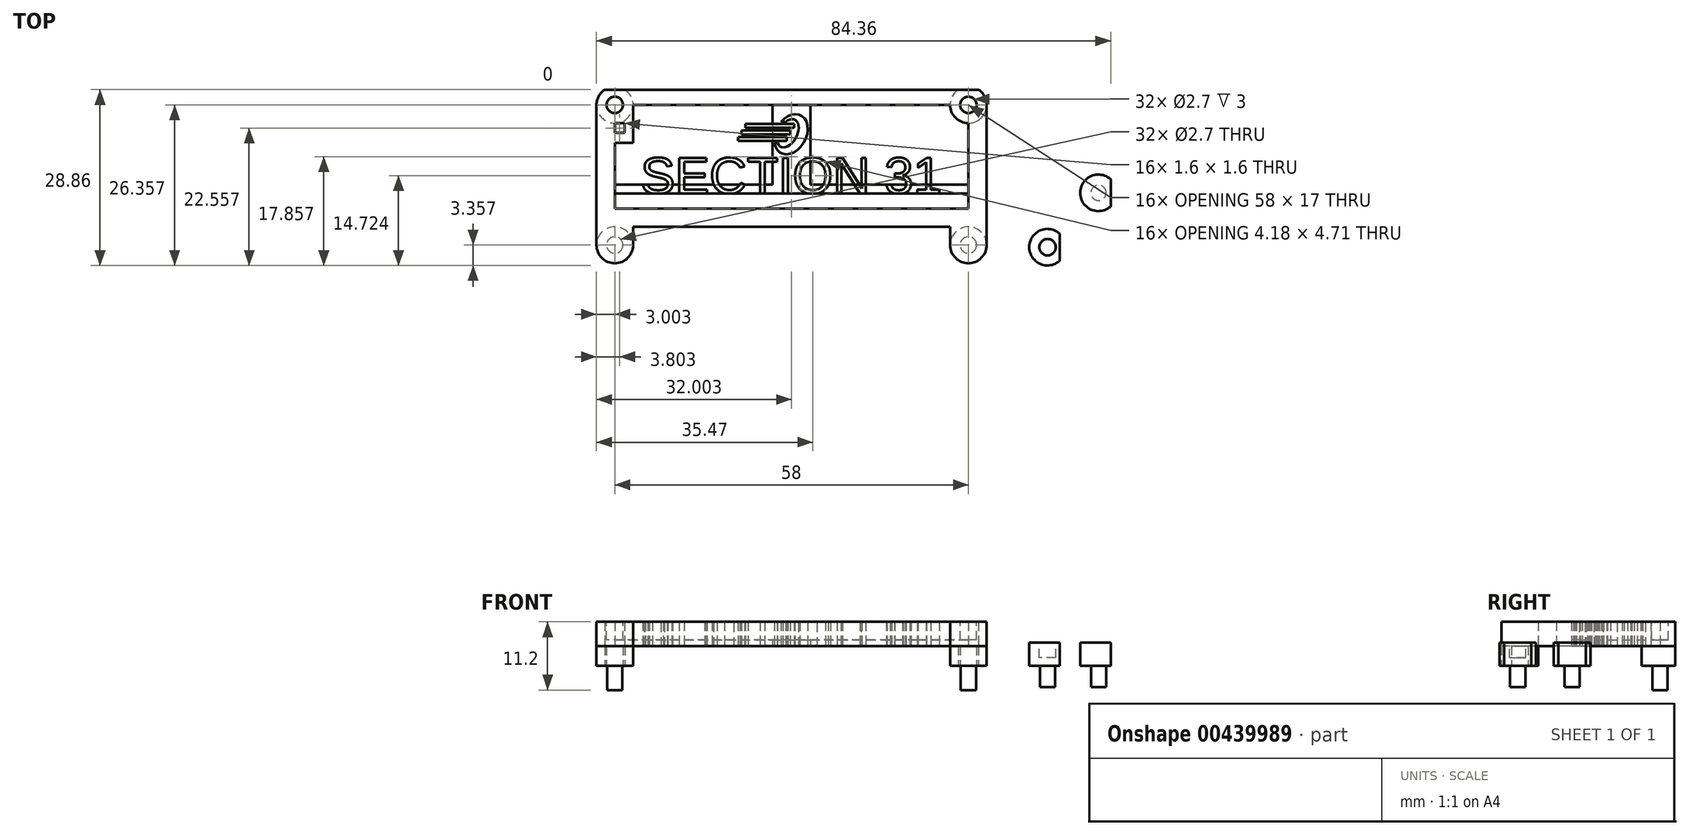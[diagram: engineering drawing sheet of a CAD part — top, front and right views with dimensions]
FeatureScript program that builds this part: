
annotation { "Feature Type Name" : "Feature", "Feature Type Description" : "" }
export const myFeature = defineFeature(function(context is Context, id is Id, definition is map)
    precondition{}
    {
        {
            var Q0;
            Q0=qCreatedBy(makeId("Top.planeOp"),FACE);
            var sketch = newSketch(context, id + "F0", { "sketchPlane" : qUnion([Q0])});
            skArc(sketch, "E0", {"start": v(2, 2.24) * mm, "mid": v(-3, 0) * mm, "end": v(2, -2.24) * mm});
            skCircle(sketch, "E1", {"center": v(0, 0) * mm, "radius": 1.25 * mm});
            skLineSegment(sketch, "E2", {"start": v(2, 2.24) * mm, "end": v(2, -2.24) * mm});
            skPoint(sketch, "E3", {"position": v(-9.49, 26.86) * mm});
            skLineSegment(sketch, "E4.bottom", {"start": v(-9.49, 26.86) * mm, "end": v(-74.49, 26.86) * mm});
            skLineSegment(sketch, "E4.top", {"start": v(-9.49, -3.14) * mm, "end": v(-74.49, -3.14) * mm});
            skLineSegment(sketch, "E4.left", {"start": v(-9.49, 26.86) * mm, "end": v(-9.49, -3.14) * mm});
            skLineSegment(sketch, "E4.right", {"start": v(-74.49, 26.86) * mm, "end": v(-74.49, -3.14) * mm});
            skLineSegment(sketch, "E5", {"start": v(-41.99, 26.86) * mm, "end": v(-41.99, -3.14) * mm, "construction": true});
            skLineSegment(sketch, "E6", {"start": v(-74.49, 11.86) * mm, "end": v(-9.49, 11.86) * mm, "construction": true});
            skPoint(sketch, "E7", {"position": v(-12.99, 23.36) * mm});
            skPoint(sketch, "E8", {"position": v(-70.99, 23.36) * mm});
            skPoint(sketch, "E9", {"position": v(-70.99, 0.36) * mm});
            skPoint(sketch, "E10", {"position": v(-12.99, 0.36) * mm});
            skArc(sketch, "E11", {"start": v(-14.65, 25.86) * mm, "mid": v(-12.99, 20.36) * mm, "end": v(-11.33, 25.86) * mm});
            skArc(sketch, "E12", {"start": v(-72.65, 25.86) * mm, "mid": v(-70.99, 20.36) * mm, "end": v(-69.33, 25.86) * mm});
            skCircle(sketch, "E13", {"center": v(-70.99, 0.36) * mm, "radius": 3 * mm});
            skCircle(sketch, "E14", {"center": v(-12.99, 0.36) * mm, "radius": 3 * mm});
            skCircle(sketch, "E15", {"center": v(-70.99, 23.36) * mm, "radius": 1.25 * mm});
            skCircle(sketch, "E16", {"center": v(-12.99, 23.36) * mm, "radius": 1.25 * mm});
            skCircle(sketch, "E17", {"center": v(-70.99, 0.36) * mm, "radius": 1.35 * mm});
            skCircle(sketch, "E18", {"center": v(-12.99, 0.36) * mm, "radius": 1.35 * mm});
            skLineSegment(sketch, "E19", {"start": v(-72.65, 25.86) * mm, "end": v(-69.33, 25.86) * mm});
            skLineSegment(sketch, "E20", {"start": v(-14.65, 25.86) * mm, "end": v(-11.33, 25.86) * mm});
            skArc(sketch, "E21", {"start": v(10.37, 11.15) * mm, "mid": v(5.37, 8.92) * mm, "end": v(10.37, 6.68) * mm});
            skCircle(sketch, "E22", {"center": v(8.37, 8.92) * mm, "radius": 1.25 * mm});
            skLineSegment(sketch, "E23", {"start": v(10.37, 11.15) * mm, "end": v(10.37, 6.68) * mm});
            skSolve(sketch);
        }
        {
            var Q0;
            Q0=makeQuery(id+"F0.imprint","IMPRINT",FACE,{"disambiguationData":[TD([[makeQuery(id+"F0.imprint","IMPRINT",EDGE,{"derivedFrom":sQuery(id+"F0.wireOp",EDGE,"E1")}),1.0]])]});
            var Q1;
            Q1=makeQuery(id+"F0.imprint","IMPRINT",FACE,{"disambiguationData":[TD([[makeQuery(id+"F0.imprint","IMPRINT",EDGE,{"derivedFrom":sQuery(id+"F0.wireOp",EDGE,"E1")}),-1.0]])]});
            var Q2;
            Q2=makeQuery(id+"F0.imprint","IMPRINT",FACE,{"disambiguationData":[TD([[makeQuery(id+"F0.imprint","IMPRINT",EDGE,{"derivedFrom":sQuery(id+"F0.wireOp",EDGE,"E22")}),1.0]])]});
            var Q3;
            Q3=makeQuery(id+"F0.imprint","IMPRINT",FACE,{"disambiguationData":[TD([[makeQuery(id+"F0.imprint","IMPRINT",EDGE,{"derivedFrom":sQuery(id+"F0.wireOp",EDGE,"E21")}),1.0]])]});
            extrude(context, id + "F1", {"entities" : qUnion([Q0, Q1, Q2, Q3]), "depth" : 3.8 * mm});
        }
        {
            var Q0;
            Q0=makeQuery(id+"F1.opExtrude","CAP_FACE",FACE,{"disambiguationData":[OSD([sQuery(id+"F0.wireOp",EDGE,"E0")])],"isStart":false});
            var sketch = newSketch(context, id + "F2", { "sketchPlane" : qUnion([Q0])});
            skCircle(sketch, "E24", {"center": v(0, 0) * mm, "radius": 1 * mm});
            skSolve(sketch);
        }
        {
            var Q0;
            Q0=makeQuery(id+"F0.imprint","IMPRINT",FACE,{"disambiguationData":[TD([[makeQuery(id+"F0.imprint","IMPRINT",EDGE,{"derivedFrom":sQuery(id+"F0.wireOp",EDGE,"E16")}),-1.0]])]});
            var Q1;
            Q1=makeQuery(id+"F0.imprint","IMPRINT",FACE,{"disambiguationData":[TD([[makeQuery(id+"F0.imprint","IMPRINT",EDGE,{"derivedFrom":sQuery(id+"F0.wireOp",EDGE,"E16")}),1.0]])]});
            var Q2;
            Q2=makeQuery(id+"F0.imprint","IMPRINT",FACE,{"disambiguationData":[TD([[makeQuery(id+"F0.imprint","IMPRINT",EDGE,{"derivedFrom":sQuery(id+"F0.wireOp",EDGE,"E15")}),-1.0]])]});
            var Q3;
            Q3=makeQuery(id+"F0.imprint","IMPRINT",FACE,{"disambiguationData":[TD([[makeQuery(id+"F0.imprint","IMPRINT",EDGE,{"derivedFrom":sQuery(id+"F0.wireOp",EDGE,"E15")}),1.0]])]});
            var Q4;
            Q4=makeQuery(id+"F0.imprint","IMPRINT",FACE,{"disambiguationData":[TD([[makeQuery(id+"F0.imprint","IMPRINT",EDGE,{"derivedFrom":sQuery(id+"F0.wireOp",EDGE,"E13")}),1.0]])]});
            var Q5;
            Q5=makeQuery(id+"F0.imprint","IMPRINT",FACE,{"disambiguationData":[TD([[makeQuery(id+"F0.imprint","IMPRINT",EDGE,{"derivedFrom":sQuery(id+"F0.wireOp",EDGE,"E14")}),1.0]])]});
            extrude(context, id + "F3", {"entities" : qUnion([Q0, Q1, Q2, Q3, Q4, Q5]), "depth" : 3.2 * mm});
        }
        {
            var Q0;
            Q0=makeQuery(id+"F3.opExtrude","CAP_FACE",FACE,{"disambiguationData":[OSD([sQuery(id+"F0.wireOp",EDGE,"E12"),sQuery(id+"F0.wireOp",EDGE,"E19")])],"isStart":false});
            var sketch = newSketch(context, id + "F4", { "sketchPlane" : qUnion([Q0])});
            skArc(sketch, "E25.1.0", {"start": v(-14.65, 25.86) * mm, "mid": v(-12.99, 20.36) * mm, "end": v(-11.33, 25.86) * mm});
            skLineSegment(sketch, "E25.1.1", {"start": v(-11.33, 25.86) * mm, "end": v(-14.65, 25.86) * mm});
            skCircle(sketch, "E25.2", {"center": v(-12.99, 0.36) * mm, "radius": 3 * mm});
            skCircle(sketch, "E25.3", {"center": v(-70.99, 0.36) * mm, "radius": 3 * mm});
            skPoint(sketch, "E26", {"position": v(-70.99, 23.36) * mm});
            skPoint(sketch, "E27", {"position": v(-73.99, 23.36) * mm});
            skPoint(sketch, "E28", {"position": v(-73.99, 0.36) * mm});
            skPoint(sketch, "E29", {"position": v(-9.99, 23.36) * mm});
            skPoint(sketch, "E30", {"position": v(-9.99, 0.36) * mm});
            skLineSegment(sketch, "E31", {"start": v(-73.99, 23.36) * mm, "end": v(-73.99, 0.36) * mm});
            skLineSegment(sketch, "E32", {"start": v(-9.99, 23.36) * mm, "end": v(-9.99, 0.36) * mm});
            skLineSegment(sketch, "E33", {"start": v(-69.33, 25.86) * mm, "end": v(-14.65, 25.86) * mm});
            skLineSegment(sketch, "E34", {"start": v(-70.99, 20.36) * mm, "end": v(-70.99, 6.36) * mm});
            skLineSegment(sketch, "E35", {"start": v(-12.99, 20.36) * mm, "end": v(-12.99, 6.36) * mm});
            skLineSegment(sketch, "E36", {"start": v(-67.99, 23.36) * mm, "end": v(-15.99, 23.36) * mm});
            skLineSegment(sketch, "E37", {"start": v(-67.99, 0.36) * mm, "end": v(-67.99, 3.36) * mm});
            skLineSegment(sketch, "E38", {"start": v(-67.99, 3.36) * mm, "end": v(-67.99, 6.36) * mm});
            skLineSegment(sketch, "E39", {"start": v(-67.99, 6.36) * mm, "end": v(-70.99, 6.36) * mm});
            skPoint(sketch, "E40", {"position": v(-15.99, 0.36) * mm});
            skPoint(sketch, "E41", {"position": v(-12.99, 3.36) * mm});
            skPoint(sketch, "E42", {"position": v(-15.99, 3.36) * mm});
            skLineSegment(sketch, "E43", {"start": v(-15.99, 0.36) * mm, "end": v(-15.99, 3.36) * mm});
            skLineSegment(sketch, "E44", {"start": v(-15.99, 3.36) * mm, "end": v(-15.99, 6.36) * mm});
            skLineSegment(sketch, "E45", {"start": v(-12.99, 6.36) * mm, "end": v(-15.99, 6.36) * mm});
            skPoint(sketch, "E46.orphan", {"position": v(-70.99, 3.36) * mm});
            skLineSegment(sketch, "E47", {"start": v(-67.99, 6.36) * mm, "end": v(-15.99, 6.36) * mm});
            skLineSegment(sketch, "E48", {"start": v(-67.99, 3.36) * mm, "end": v(-15.99, 3.36) * mm});
            skText(sketch, "E49", { "text": "SECTION 31", "fontName": "Arimo-Regular.ttf"});
            skEllipticalArc(sketch, "E50", {});
            skEllipticalArc(sketch, "E51", {});
            skLineSegment(sketch, "E52", {"start": v(-42.99, 20.54) * mm, "end": v(-43.74, 20.54) * mm});
            skLineSegment(sketch, "E53", {"start": v(-44.27, 17.13) * mm, "end": v(-44.8, 17.13) * mm});
            skLineSegment(sketch, "E54.bottom", {"start": v(-49.6, 20.2) * mm, "end": v(-41.6, 20.2) * mm});
            skLineSegment(sketch, "E54.top", {"start": v(-49.6, 19.6) * mm, "end": v(-41.6, 19.6) * mm});
            skLineSegment(sketch, "E54.left", {"start": v(-49.6, 20.2) * mm, "end": v(-49.6, 19.6) * mm});
            skLineSegment(sketch, "E54.right", {"start": v(-41.6, 20.2) * mm, "end": v(-41.6, 19.6) * mm});
            skLineSegment(sketch, "E55.0.1.0", {"start": v(-50.18, 18.53) * mm, "end": v(-42.18, 18.53) * mm});
            skLineSegment(sketch, "E55.0.1.1", {"start": v(-50.18, 19.13) * mm, "end": v(-42.18, 19.13) * mm});
            skLineSegment(sketch, "E55.0.1.2", {"start": v(-50.18, 19.13) * mm, "end": v(-50.18, 18.53) * mm});
            skLineSegment(sketch, "E55.0.1.3", {"start": v(-42.18, 19.13) * mm, "end": v(-42.18, 18.53) * mm});
            skLineSegment(sketch, "E55.0.2.0", {"start": v(-50.77, 17.45) * mm, "end": v(-42.77, 17.45) * mm});
            skLineSegment(sketch, "E55.0.2.1", {"start": v(-50.77, 18.05) * mm, "end": v(-42.77, 18.05) * mm});
            skLineSegment(sketch, "E55.0.2.2", {"start": v(-50.77, 18.05) * mm, "end": v(-50.77, 17.45) * mm});
            skLineSegment(sketch, "E55.0.2.3", {"start": v(-42.77, 18.05) * mm, "end": v(-42.77, 17.45) * mm});
            skLineSegment(sketch, "E55.direction1", {"start": v(-49.6, 19.6) * mm, "end": v(-78.1, 20.1) * mm, "construction": true});
            skLineSegment(sketch, "E55.direction2", {"start": v(-49.6, 19.6) * mm, "end": v(-50.18, 18.53) * mm, "construction": true});
            skLineSegment(sketch, "E56", {"start": v(-70.99, 10.3) * mm, "end": v(-12.99, 10.3) * mm});
            skLineSegment(sketch, "E57", {"start": v(-12.99, 10.3) * mm, "end": v(-12.99, 8.81) * mm});
            skLineSegment(sketch, "E58", {"start": v(-12.99, 8.81) * mm, "end": v(-70.99, 8.81) * mm});
            skLineSegment(sketch, "E59", {"start": v(-45.1, 23.36) * mm, "end": v(-45.1, 10.3) * mm});
            skLineSegment(sketch, "E60", {"start": v(-45.1, 10.3) * mm, "end": v(-38.87, 10.3) * mm});
            skLineSegment(sketch, "E61", {"start": v(-38.87, 10.3) * mm, "end": v(-38.87, 23.36) * mm});
            skLineSegment(sketch, "E62.bottom", {"start": v(-70.99, 20.36) * mm, "end": v(-69.39, 20.36) * mm});
            skLineSegment(sketch, "E62.top", {"start": v(-70.99, 18.76) * mm, "end": v(-69.39, 18.76) * mm});
            skLineSegment(sketch, "E62.left", {"start": v(-70.99, 20.36) * mm, "end": v(-70.99, 18.76) * mm});
            skLineSegment(sketch, "E62.right", {"start": v(-69.39, 20.82) * mm, "end": v(-69.39, 18.76) * mm});
            skArc(sketch, "E63.0", {"start": v(-72.65, 25.86) * mm, "mid": v(-70.99, 20.36) * mm, "end": v(-69.33, 25.86) * mm});
            skLineSegment(sketch, "E64", {"start": v(-67.99, 23.36) * mm, "end": v(-67.99, 17.16) * mm});
            skLineSegment(sketch, "E65", {"start": v(-70.99, 17.16) * mm, "end": v(-67.99, 17.16) * mm});
            const initialGuessF4  = {"E49": [-0.06676, 0.00881, 1, 0, 0.0061], "E50": [-0.04208758574724197, 0.018540096214413642, 0.47281776343246007, 0.8811602366100767, 0.0035, 0.0025, 2.3784830967176416, 1.286216884327917], "E51": [-0.042587585747241974, 0.018690096214413643, 0.4728177634324602, 0.8811602366100766, 0.0025, 0.0015, 2.623059062491213, 0.955721149236281]};
            skSetInitialGuess(sketch, initialGuessF4);
            skSolve(sketch);
        }
        {
            var Q0;
            {var subQ0=sQuery(id+"F4.wireOp",EDGE,"E56");var subQ1=sQuery(id+"F4.wireOp",EDGE,"E34");var subQ2=makeQuery(id+"F4.imprint","INTERSECT",VERTEX,{"derivedFrom":[subQ1,subQ0]});Q0=makeQuery(id+"F4.imprint","IMPRINT",FACE,{"disambiguationData":[TD([[makeQuery(id+"F4.imprint","IMPRINT",EDGE,{"disambiguationData":[TD([[subQ2,-1.0]])],"derivedFrom":subQ1}),1.0]])]});}
            var Q1;
            {var subQ10=sQuery(id+"F4.wireOp",EDGE,"E49.sketch_text.stroke-5");Q1=makeQuery(id+"F4.imprint","IMPRINT",FACE,{"disambiguationData":[TD([[makeQuery(id+"F4.imprint","IMPRINT",EDGE,{"derivedFrom":subQ10}),-1.0]])]});}
            var Q2;
            {var subQ4=sQuery(id+"F4.wireOp",EDGE,"E49.sketch_text.stroke-5");Q2=makeQuery(id+"F4.imprint","IMPRINT",FACE,{"disambiguationData":[TD([[makeQuery(id+"F4.imprint","IMPRINT",EDGE,{"derivedFrom":subQ4}),1.0]])]});}
            var Q3;
            {var subQ1=sQuery(id+"F4.wireOp",EDGE,"E49.sketch_text.stroke-0");var subQ5=sQuery(id+"F4.wireOp",EDGE,"E49.sketch_text.stroke-1");var subQ6=makeQuery(id+"F4.imprint","INTERSECT",VERTEX,{"derivedFrom":[subQ1,subQ5]});Q3=makeQuery(id+"F4.imprint","IMPRINT",FACE,{"disambiguationData":[TD([[makeQuery(id+"F4.imprint","IMPRINT",EDGE,{"disambiguationData":[TD([[subQ6,1.0]])],"derivedFrom":subQ1}),1.0]])]});}
            var Q4;
            {var subQ1=sQuery(id+"F4.wireOp",EDGE,"E49.sketch_text.stroke-43");Q4=makeQuery(id+"F4.imprint","IMPRINT",FACE,{"disambiguationData":[TD([[makeQuery(id+"F4.imprint","IMPRINT",EDGE,{"derivedFrom":subQ1}),-1.0]])]});}
            var Q5;
            {var subQ5=sQuery(id+"F4.wireOp",EDGE,"E49.sketch_text.stroke-43");Q5=makeQuery(id+"F4.imprint","IMPRINT",FACE,{"disambiguationData":[TD([[makeQuery(id+"F4.imprint","IMPRINT",EDGE,{"derivedFrom":subQ5}),1.0]])]});}
            var Q6;
            {var subQ12=sQuery(id+"F4.wireOp",EDGE,"E49.sketch_text.stroke-49");Q6=makeQuery(id+"F4.imprint","IMPRINT",FACE,{"disambiguationData":[TD([[makeQuery(id+"F4.imprint","IMPRINT",EDGE,{"derivedFrom":subQ12}),-1.0]])]});}
            var Q7;
            {var subQ0=sQuery(id+"F4.wireOp",EDGE,"E49.sketch_text.stroke-49");Q7=makeQuery(id+"F4.imprint","IMPRINT",FACE,{"disambiguationData":[TD([[makeQuery(id+"F4.imprint","IMPRINT",EDGE,{"derivedFrom":subQ0}),1.0]])]});}
            var Q8;
            {var subQ6=sQuery(id+"F4.wireOp",EDGE,"E49.sketch_text.stroke-52");Q8=makeQuery(id+"F4.imprint","IMPRINT",FACE,{"disambiguationData":[TD([[makeQuery(id+"F4.imprint","IMPRINT",EDGE,{"derivedFrom":subQ6}),1.0]])]});}
            var Q9;
            {var subQ0=sQuery(id+"F4.wireOp",EDGE,"E58");var subQ1=sQuery(id+"F4.wireOp",EDGE,"E49.sketch_text.stroke-64");var subQ2=makeQuery(id+"F4.imprint","INTERSECT",VERTEX,{"derivedFrom":[subQ1,subQ0]});Q9=makeQuery(id+"F4.imprint","IMPRINT",FACE,{"disambiguationData":[TD([[makeQuery(id+"F4.imprint","IMPRINT",EDGE,{"disambiguationData":[TD([[subQ2,1.0]])],"derivedFrom":subQ1}),-1.0]])]});}
            var Q10;
            {var subQ0=sQuery(id+"F4.wireOp",EDGE,"E58");var subQ1=sQuery(id+"F4.wireOp",EDGE,"E49.sketch_text.stroke-64");var subQ2=makeQuery(id+"F4.imprint","INTERSECT",VERTEX,{"derivedFrom":[subQ1,subQ0]});Q10=makeQuery(id+"F4.imprint","IMPRINT",FACE,{"disambiguationData":[TD([[makeQuery(id+"F4.imprint","IMPRINT",EDGE,{"disambiguationData":[TD([[subQ2,1.0]])],"derivedFrom":subQ1}),1.0]])]});}
            var Q11;
            {var subQ0=sQuery(id+"F4.wireOp",EDGE,"E58");var subQ1=sQuery(id+"F4.wireOp",EDGE,"E49.sketch_text.stroke-72");var subQ2=makeQuery(id+"F4.imprint","INTERSECT",VERTEX,{"derivedFrom":[subQ1,subQ0]});Q11=makeQuery(id+"F4.imprint","IMPRINT",FACE,{"disambiguationData":[TD([[makeQuery(id+"F4.imprint","IMPRINT",EDGE,{"disambiguationData":[TD([[subQ2,-1.0]])],"derivedFrom":subQ1}),-1.0]])]});}
            var Q12;
            {var subQ1=sQuery(id+"F4.wireOp",EDGE,"E49.sketch_text.stroke-80");Q12=makeQuery(id+"F4.imprint","IMPRINT",FACE,{"disambiguationData":[TD([[makeQuery(id+"F4.imprint","IMPRINT",EDGE,{"derivedFrom":subQ1}),1.0]])]});}
            var Q13;
            {var subQ7=sQuery(id+"F4.wireOp",EDGE,"E49.sketch_text.stroke-77");Q13=makeQuery(id+"F4.imprint","IMPRINT",FACE,{"disambiguationData":[TD([[makeQuery(id+"F4.imprint","IMPRINT",EDGE,{"derivedFrom":subQ7}),-1.0]])]});}
            var Q14;
            {var subQ4=sQuery(id+"F4.wireOp",EDGE,"E49.sketch_text.stroke-92");Q14=makeQuery(id+"F4.imprint","IMPRINT",FACE,{"disambiguationData":[TD([[makeQuery(id+"F4.imprint","IMPRINT",EDGE,{"derivedFrom":subQ4}),1.0]])]});}
            var Q15;
            {var subQ6=sQuery(id+"F4.wireOp",EDGE,"E49.sketch_text.stroke-77");Q15=makeQuery(id+"F4.imprint","IMPRINT",FACE,{"disambiguationData":[TD([[makeQuery(id+"F4.imprint","IMPRINT",EDGE,{"derivedFrom":subQ6}),1.0]])]});}
            var Q16;
            {var subQ0=sQuery(id+"F4.wireOp",EDGE,"E58");var subQ1=sQuery(id+"F4.wireOp",EDGE,"E49.sketch_text.stroke-98");var subQ2=makeQuery(id+"F4.imprint","INTERSECT",VERTEX,{"derivedFrom":[subQ1,subQ0]});Q16=makeQuery(id+"F4.imprint","IMPRINT",FACE,{"disambiguationData":[TD([[makeQuery(id+"F4.imprint","IMPRINT",EDGE,{"disambiguationData":[TD([[subQ2,1.0]])],"derivedFrom":subQ1}),-1.0]])]});}
            var Q17;
            {var subQ0=sQuery(id+"F4.wireOp",EDGE,"E58");var subQ1=sQuery(id+"F4.wireOp",EDGE,"E49.sketch_text.stroke-95");var subQ2=makeQuery(id+"F4.imprint","INTERSECT",VERTEX,{"derivedFrom":[subQ1,subQ0]});Q17=makeQuery(id+"F4.imprint","IMPRINT",FACE,{"disambiguationData":[TD([[makeQuery(id+"F4.imprint","IMPRINT",EDGE,{"disambiguationData":[TD([[subQ2,-1.0]])],"derivedFrom":subQ1}),1.0]])]});}
            var Q18;
            {var subQ0=sQuery(id+"F4.wireOp",EDGE,"E58");var subQ5=sQuery(id+"F4.wireOp",EDGE,"E49.sketch_text.stroke-95");var subQ12=makeQuery(id+"F4.imprint","INTERSECT",VERTEX,{"derivedFrom":[subQ5,subQ0]});Q18=makeQuery(id+"F4.imprint","IMPRINT",FACE,{"disambiguationData":[TD([[makeQuery(id+"F4.imprint","IMPRINT",EDGE,{"disambiguationData":[TD([[subQ12,-1.0]])],"derivedFrom":subQ5}),-1.0]])]});}
            var Q19;
            {var subQ0=sQuery(id+"F4.wireOp",EDGE,"E49.sketch_text.stroke-103");var subQ1=sQuery(id+"F4.wireOp",EDGE,"E49.sketch_text.stroke-102");var subQ2=makeQuery(id+"F4.imprint","INTERSECT",VERTEX,{"derivedFrom":[subQ1,subQ0]});Q19=makeQuery(id+"F4.imprint","IMPRINT",FACE,{"disambiguationData":[TD([[makeQuery(id+"F4.imprint","IMPRINT",EDGE,{"disambiguationData":[TD([[subQ2,1.0]])],"derivedFrom":subQ1}),1.0]])]});}
            var Q20;
            {var subQ5=sQuery(id+"F4.wireOp",EDGE,"E49.sketch_text.stroke-106");var subQ7=sQuery(id+"F4.wireOp",EDGE,"E58");var subQ9=makeQuery(id+"F4.imprint","INTERSECT",VERTEX,{"derivedFrom":[subQ5,subQ7]});Q20=makeQuery(id+"F4.imprint","IMPRINT",FACE,{"disambiguationData":[TD([[makeQuery(id+"F4.imprint","IMPRINT",EDGE,{"disambiguationData":[TD([[subQ9,1.0]])],"derivedFrom":subQ5}),1.0]])]});}
            var Q21;
            {var subQ0=sQuery(id+"F4.wireOp",EDGE,"E49.sketch_text.stroke-114");Q21=makeQuery(id+"F4.imprint","IMPRINT",FACE,{"disambiguationData":[TD([[makeQuery(id+"F4.imprint","IMPRINT",EDGE,{"derivedFrom":subQ0}),1.0]])]});}
            var Q22;
            {var subQ14=sQuery(id+"F4.wireOp",EDGE,"E49.sketch_text.stroke-114");Q22=makeQuery(id+"F4.imprint","IMPRINT",FACE,{"disambiguationData":[TD([[makeQuery(id+"F4.imprint","IMPRINT",EDGE,{"derivedFrom":subQ14}),-1.0]])]});}
            var Q23;
            {var subQ0=sQuery(id+"F4.wireOp",EDGE,"E49.sketch_text.stroke-137");Q23=makeQuery(id+"F4.imprint","IMPRINT",FACE,{"disambiguationData":[TD([[makeQuery(id+"F4.imprint","IMPRINT",EDGE,{"derivedFrom":subQ0}),1.0]])]});}
            var Q24;
            {var subQ5=sQuery(id+"F4.wireOp",EDGE,"E49.sketch_text.stroke-137");Q24=makeQuery(id+"F4.imprint","IMPRINT",FACE,{"disambiguationData":[TD([[makeQuery(id+"F4.imprint","IMPRINT",EDGE,{"derivedFrom":subQ5}),-1.0]])]});}
            var Q25;
            {var subQ6=sQuery(id+"F4.wireOp",EDGE,"E49.sketch_text.stroke-145");Q25=makeQuery(id+"F4.imprint","IMPRINT",FACE,{"disambiguationData":[TD([[makeQuery(id+"F4.imprint","IMPRINT",EDGE,{"derivedFrom":subQ6}),1.0]])]});}
            var Q26;
            {var subQ16=sQuery(id+"F4.wireOp",EDGE,"E49.sketch_text.stroke-70");Q26=makeQuery(id+"F4.imprint","IMPRINT",FACE,{"disambiguationData":[TD([[makeQuery(id+"F4.imprint","IMPRINT",EDGE,{"derivedFrom":subQ16}),1.0]])]});}
            var Q27;
            {var subQ5=sQuery(id+"F4.wireOp",EDGE,"E49.sketch_text.stroke-90");Q27=makeQuery(id+"F4.imprint","IMPRINT",FACE,{"disambiguationData":[TD([[makeQuery(id+"F4.imprint","IMPRINT",EDGE,{"derivedFrom":subQ5}),1.0]])]});}
            var Q28;
            {var subQ1=sQuery(id+"F4.wireOp",EDGE,"E49.sketch_text.stroke-82");Q28=makeQuery(id+"F4.imprint","IMPRINT",FACE,{"disambiguationData":[TD([[makeQuery(id+"F4.imprint","IMPRINT",EDGE,{"derivedFrom":subQ1}),-1.0]])]});}
            var Q29;
            {var subQ0=sQuery(id+"F4.wireOp",EDGE,"E49.sketch_text.stroke-73");Q29=makeQuery(id+"F4.imprint","IMPRINT",FACE,{"disambiguationData":[TD([[makeQuery(id+"F4.imprint","IMPRINT",EDGE,{"derivedFrom":subQ0}),-1.0]])]});}
            var Q30;
            {var subQ0=sQuery(id+"F4.wireOp",EDGE,"E49.sketch_text.stroke-70");Q30=makeQuery(id+"F4.imprint","IMPRINT",FACE,{"disambiguationData":[TD([[makeQuery(id+"F4.imprint","IMPRINT",EDGE,{"derivedFrom":subQ0}),-1.0]])]});}
            var Q31;
            Q31=makeQuery(id+"F4.imprint","IMPRINT",FACE,{"disambiguationData":[TD([[makeQuery(id+"F4.imprint","IMPRINT",EDGE,{"derivedFrom":sQuery(id+"F4.wireOp",EDGE,"E50")}),1.0]])]});
            var Q32;
            {var subQ0=sQuery(id+"F4.wireOp",EDGE,"E55.0.2.3");Q32=makeQuery(id+"F4.imprint","IMPRINT",FACE,{"disambiguationData":[TD([[makeQuery(id+"F4.imprint","IMPRINT",EDGE,{"derivedFrom":subQ0}),-1.0]])]});}
            var Q33;
            {var subQ0=sQuery(id+"F4.wireOp",EDGE,"E55.0.1.3");Q33=makeQuery(id+"F4.imprint","IMPRINT",FACE,{"disambiguationData":[TD([[makeQuery(id+"F4.imprint","IMPRINT",EDGE,{"derivedFrom":subQ0}),-1.0]])]});}
            var Q34;
            {var subQ0=sQuery(id+"F4.wireOp",EDGE,"E54.right");Q34=makeQuery(id+"F4.imprint","IMPRINT",FACE,{"disambiguationData":[TD([[makeQuery(id+"F4.imprint","IMPRINT",EDGE,{"derivedFrom":subQ0}),-1.0]])]});}
            extrude(context, id + "F5", {"entities" : qUnion([Q0, Q1, Q2, Q3, Q4, Q5, Q6, Q7, Q8, Q9, Q10, Q11, Q12, Q13, Q14, Q15, Q16, Q17, Q18, Q19, Q20, Q21, Q22, Q23, Q24, Q25, Q26, Q27, Q28, Q29, Q30, Q31, Q32, Q33, Q34]), "depth" : 1 * mm});
        }
        {
            var Q0;
            {var subQ4=sQuery(id+"F4.wireOp",EDGE,"E32");Q0=makeQuery(id+"F4.imprint","IMPRINT",FACE,{"disambiguationData":[TD([[makeQuery(id+"F4.imprint","IMPRINT",EDGE,{"derivedFrom":subQ4}),-1.0]])]});}
            var Q1;
            {var subQ0=sQuery(id+"F4.wireOp",EDGE,"E25.2");var subQ1=makeQuery(id+"F4.imprint","INTERSECT",VERTEX,{"derivedFrom":[subQ0,sQuery(id+"F4.wireOp",EDGE,"E32")]});Q1=makeQuery(id+"F4.imprint","IMPRINT",FACE,{"disambiguationData":[TD([[makeQuery(id+"F4.imprint","IMPRINT",EDGE,{"disambiguationData":[TD([[subQ1,-1.0]])],"derivedFrom":subQ0}),1.0]])]});}
            var Q2;
            {var subQ0=sQuery(id+"F4.wireOp",EDGE,"E25.1.1");Q2=makeQuery(id+"F4.imprint","IMPRINT",FACE,{"disambiguationData":[TD([[makeQuery(id+"F4.imprint","IMPRINT",EDGE,{"derivedFrom":subQ0}),1.0]])]});}
            var Q3;
            {var subQ5=sQuery(id+"F4.wireOp",EDGE,"E33");Q3=makeQuery(id+"F4.imprint","IMPRINT",FACE,{"disambiguationData":[TD([[makeQuery(id+"F4.imprint","IMPRINT",EDGE,{"derivedFrom":subQ5}),-1.0]])]});}
            var Q4;
            {var subQ3=makeQuery(id+"F3.opExtrude","CAP_EDGE",EDGE,{"disambiguationData":[OSD([sQuery(id+"F0.wireOp",EDGE,"E19")])],"isStart":false});Q4=makeQuery(id+"F4.imprint","IMPRINT",FACE,{"disambiguationData":[TD([[makeQuery(id+"F4.imprint","IMPRINT",EDGE,{"derivedFrom":subQ3}),-1.0]])]});}
            var Q5;
            {var subQ3=sQuery(id+"F4.wireOp",EDGE,"E31");Q5=makeQuery(id+"F4.imprint","IMPRINT",FACE,{"disambiguationData":[TD([[makeQuery(id+"F4.imprint","IMPRINT",EDGE,{"derivedFrom":subQ3}),1.0]])]});}
            var Q6;
            {var subQ0=sQuery(id+"F4.wireOp",EDGE,"E25.3");var subQ1=makeQuery(id+"F4.imprint","INTERSECT",VERTEX,{"derivedFrom":[subQ0,sQuery(id+"F4.wireOp",EDGE,"E31")]});Q6=makeQuery(id+"F4.imprint","IMPRINT",FACE,{"disambiguationData":[TD([[makeQuery(id+"F4.imprint","IMPRINT",EDGE,{"disambiguationData":[TD([[subQ1,1.0]])],"derivedFrom":subQ0}),1.0]])]});}
            var Q7;
            Q7=makeQuery(id+"F4.imprint","IMPRINT",FACE,{"disambiguationData":[TD([[makeQuery(id+"F4.imprint","IMPRINT",EDGE,{"derivedFrom":sQuery(id+"F4.wireOp",EDGE,"E38")}),-1.0]])]});
            var Q8;
            {var subQ0=sQuery(id+"F4.wireOp",EDGE,"E55.0.2.2");Q8=makeQuery(id+"F4.imprint","IMPRINT",FACE,{"disambiguationData":[TD([[makeQuery(id+"F4.imprint","IMPRINT",EDGE,{"derivedFrom":subQ0}),1.0]])]});}
            var Q9;
            {var subQ0=sQuery(id+"F4.wireOp",EDGE,"E55.0.1.2");Q9=makeQuery(id+"F4.imprint","IMPRINT",FACE,{"disambiguationData":[TD([[makeQuery(id+"F4.imprint","IMPRINT",EDGE,{"derivedFrom":subQ0}),1.0]])]});}
            var Q10;
            {var subQ0=sQuery(id+"F4.wireOp",EDGE,"E54.left");Q10=makeQuery(id+"F4.imprint","IMPRINT",FACE,{"disambiguationData":[TD([[makeQuery(id+"F4.imprint","IMPRINT",EDGE,{"derivedFrom":subQ0}),1.0]])]});}
            var Q11;
            {var subQ0=sQuery(id+"F4.wireOp",EDGE,"E54.right");Q11=makeQuery(id+"F4.imprint","IMPRINT",FACE,{"disambiguationData":[TD([[makeQuery(id+"F4.imprint","IMPRINT",EDGE,{"derivedFrom":subQ0}),-1.0]])]});}
            var Q12;
            {var subQ0=sQuery(id+"F4.wireOp",EDGE,"E55.0.1.3");Q12=makeQuery(id+"F4.imprint","IMPRINT",FACE,{"disambiguationData":[TD([[makeQuery(id+"F4.imprint","IMPRINT",EDGE,{"derivedFrom":subQ0}),-1.0]])]});}
            var Q13;
            {var subQ0=sQuery(id+"F4.wireOp",EDGE,"E55.0.2.3");Q13=makeQuery(id+"F4.imprint","IMPRINT",FACE,{"disambiguationData":[TD([[makeQuery(id+"F4.imprint","IMPRINT",EDGE,{"derivedFrom":subQ0}),-1.0]])]});}
            var Q14;
            Q14=makeQuery(id+"F4.imprint","IMPRINT",FACE,{"disambiguationData":[TD([[makeQuery(id+"F4.imprint","IMPRINT",EDGE,{"derivedFrom":sQuery(id+"F4.wireOp",EDGE,"E50")}),1.0]])]});
            var Q15;
            {var subQ1=sQuery(id+"F4.wireOp",EDGE,"E49.sketch_text.stroke-82");Q15=makeQuery(id+"F4.imprint","IMPRINT",FACE,{"disambiguationData":[TD([[makeQuery(id+"F4.imprint","IMPRINT",EDGE,{"derivedFrom":subQ1}),-1.0]])]});}
            var Q16;
            {var subQ9=sQuery(id+"F4.wireOp",EDGE,"E49.sketch_text.stroke-84");Q16=makeQuery(id+"F4.imprint","IMPRINT",FACE,{"disambiguationData":[TD([[makeQuery(id+"F4.imprint","IMPRINT",EDGE,{"derivedFrom":subQ9}),-1.0]])]});}
            var Q17;
            {var subQ7=sQuery(id+"F4.wireOp",EDGE,"E49.sketch_text.stroke-77");Q17=makeQuery(id+"F4.imprint","IMPRINT",FACE,{"disambiguationData":[TD([[makeQuery(id+"F4.imprint","IMPRINT",EDGE,{"derivedFrom":subQ7}),-1.0]])]});}
            var Q18;
            {var subQ0=sQuery(id+"F4.wireOp",EDGE,"E49.sketch_text.stroke-73");Q18=makeQuery(id+"F4.imprint","IMPRINT",FACE,{"disambiguationData":[TD([[makeQuery(id+"F4.imprint","IMPRINT",EDGE,{"derivedFrom":subQ0}),-1.0]])]});}
            var Q19;
            {var subQ0=sQuery(id+"F4.wireOp",EDGE,"E58");var subQ1=sQuery(id+"F4.wireOp",EDGE,"E49.sketch_text.stroke-72");var subQ2=makeQuery(id+"F4.imprint","INTERSECT",VERTEX,{"derivedFrom":[subQ1,subQ0]});Q19=makeQuery(id+"F4.imprint","IMPRINT",FACE,{"disambiguationData":[TD([[makeQuery(id+"F4.imprint","IMPRINT",EDGE,{"disambiguationData":[TD([[subQ2,-1.0]])],"derivedFrom":subQ1}),-1.0]])]});}
            var Q20;
            {var subQ0=sQuery(id+"F4.wireOp",EDGE,"E49.sketch_text.stroke-70");Q20=makeQuery(id+"F4.imprint","IMPRINT",FACE,{"disambiguationData":[TD([[makeQuery(id+"F4.imprint","IMPRINT",EDGE,{"derivedFrom":subQ0}),-1.0]])]});}
            var Q21;
            {var subQ0=sQuery(id+"F4.wireOp",EDGE,"E58");var subQ1=sQuery(id+"F4.wireOp",EDGE,"E49.sketch_text.stroke-64");var subQ2=makeQuery(id+"F4.imprint","INTERSECT",VERTEX,{"derivedFrom":[subQ1,subQ0]});Q21=makeQuery(id+"F4.imprint","IMPRINT",FACE,{"disambiguationData":[TD([[makeQuery(id+"F4.imprint","IMPRINT",EDGE,{"disambiguationData":[TD([[subQ2,1.0]])],"derivedFrom":subQ1}),-1.0]])]});}
            var Q22;
            {var subQ0=sQuery(id+"F4.wireOp",EDGE,"E49.sketch_text.stroke-67");Q22=makeQuery(id+"F4.imprint","IMPRINT",FACE,{"disambiguationData":[TD([[makeQuery(id+"F4.imprint","IMPRINT",EDGE,{"derivedFrom":subQ0}),-1.0]])]});}
            var Q23;
            {var subQ12=sQuery(id+"F4.wireOp",EDGE,"E49.sketch_text.stroke-49");Q23=makeQuery(id+"F4.imprint","IMPRINT",FACE,{"disambiguationData":[TD([[makeQuery(id+"F4.imprint","IMPRINT",EDGE,{"derivedFrom":subQ12}),-1.0]])]});}
            var Q24;
            {var subQ0=sQuery(id+"F4.wireOp",EDGE,"E49.sketch_text.stroke-51");var subQ1=sQuery(id+"F4.wireOp",EDGE,"E49.sketch_text.stroke-50");var subQ2=makeQuery(id+"F4.imprint","INTERSECT",VERTEX,{"derivedFrom":[subQ1,subQ0]});Q24=makeQuery(id+"F4.imprint","IMPRINT",FACE,{"disambiguationData":[TD([[makeQuery(id+"F4.imprint","IMPRINT",EDGE,{"disambiguationData":[TD([[subQ2,1.0]])],"derivedFrom":subQ1}),-1.0]])]});}
            var Q25;
            Q25=makeQuery(id+"F4.imprint","IMPRINT",FACE,{"disambiguationData":[TD([[makeQuery(id+"F4.imprint","IMPRINT",EDGE,{"derivedFrom":sQuery(id+"F4.wireOp",EDGE,"E49.sketch_text.stroke-46")}),-1.0]])]});
            var Q26;
            {var subQ1=sQuery(id+"F4.wireOp",EDGE,"E49.sketch_text.stroke-43");Q26=makeQuery(id+"F4.imprint","IMPRINT",FACE,{"disambiguationData":[TD([[makeQuery(id+"F4.imprint","IMPRINT",EDGE,{"derivedFrom":subQ1}),-1.0]])]});}
            var Q27;
            {var subQ0=sQuery(id+"F4.wireOp",EDGE,"E49.sketch_text.stroke-35");Q27=makeQuery(id+"F4.imprint","IMPRINT",FACE,{"disambiguationData":[TD([[makeQuery(id+"F4.imprint","IMPRINT",EDGE,{"derivedFrom":subQ0}),-1.0]])]});}
            var Q28;
            {var subQ10=sQuery(id+"F4.wireOp",EDGE,"E49.sketch_text.stroke-5");Q28=makeQuery(id+"F4.imprint","IMPRINT",FACE,{"disambiguationData":[TD([[makeQuery(id+"F4.imprint","IMPRINT",EDGE,{"derivedFrom":subQ10}),-1.0]])]});}
            var Q29;
            {var subQ0=sQuery(id+"F4.wireOp",EDGE,"E49.sketch_text.stroke-8");Q29=makeQuery(id+"F4.imprint","IMPRINT",FACE,{"disambiguationData":[TD([[makeQuery(id+"F4.imprint","IMPRINT",EDGE,{"derivedFrom":subQ0}),-1.0]])]});}
            var Q30;
            {var subQ0=sQuery(id+"F4.wireOp",EDGE,"E58");var subQ5=sQuery(id+"F4.wireOp",EDGE,"E49.sketch_text.stroke-95");var subQ12=makeQuery(id+"F4.imprint","INTERSECT",VERTEX,{"derivedFrom":[subQ5,subQ0]});Q30=makeQuery(id+"F4.imprint","IMPRINT",FACE,{"disambiguationData":[TD([[makeQuery(id+"F4.imprint","IMPRINT",EDGE,{"disambiguationData":[TD([[subQ12,-1.0]])],"derivedFrom":subQ5}),-1.0]])]});}
            var Q31;
            {var subQ0=sQuery(id+"F4.wireOp",EDGE,"E58");var subQ1=sQuery(id+"F4.wireOp",EDGE,"E49.sketch_text.stroke-98");var subQ2=makeQuery(id+"F4.imprint","INTERSECT",VERTEX,{"derivedFrom":[subQ1,subQ0]});Q31=makeQuery(id+"F4.imprint","IMPRINT",FACE,{"disambiguationData":[TD([[makeQuery(id+"F4.imprint","IMPRINT",EDGE,{"disambiguationData":[TD([[subQ2,1.0]])],"derivedFrom":subQ1}),-1.0]])]});}
            var Q32;
            {var subQ6=sQuery(id+"F4.wireOp",EDGE,"E49.sketch_text.stroke-96");Q32=makeQuery(id+"F4.imprint","IMPRINT",FACE,{"disambiguationData":[TD([[makeQuery(id+"F4.imprint","IMPRINT",EDGE,{"derivedFrom":subQ6}),-1.0]])]});}
            var Q33;
            {var subQ4=sQuery(id+"F4.wireOp",EDGE,"E49.sketch_text.stroke-104");Q33=makeQuery(id+"F4.imprint","IMPRINT",FACE,{"disambiguationData":[TD([[makeQuery(id+"F4.imprint","IMPRINT",EDGE,{"derivedFrom":subQ4}),-1.0]])]});}
            var Q34;
            {var subQ0=sQuery(id+"F4.wireOp",EDGE,"E49.sketch_text.stroke-116");Q34=makeQuery(id+"F4.imprint","IMPRINT",FACE,{"disambiguationData":[TD([[makeQuery(id+"F4.imprint","IMPRINT",EDGE,{"derivedFrom":subQ0}),-1.0]])]});}
            var Q35;
            {var subQ14=sQuery(id+"F4.wireOp",EDGE,"E49.sketch_text.stroke-114");Q35=makeQuery(id+"F4.imprint","IMPRINT",FACE,{"disambiguationData":[TD([[makeQuery(id+"F4.imprint","IMPRINT",EDGE,{"derivedFrom":subQ14}),-1.0]])]});}
            var Q36;
            {var subQ5=sQuery(id+"F4.wireOp",EDGE,"E49.sketch_text.stroke-137");Q36=makeQuery(id+"F4.imprint","IMPRINT",FACE,{"disambiguationData":[TD([[makeQuery(id+"F4.imprint","IMPRINT",EDGE,{"derivedFrom":subQ5}),-1.0]])]});}
            var Q37;
            {var subQ5=sQuery(id+"F4.wireOp",EDGE,"E49.sketch_text.stroke-140");Q37=makeQuery(id+"F4.imprint","IMPRINT",FACE,{"disambiguationData":[TD([[makeQuery(id+"F4.imprint","IMPRINT",EDGE,{"derivedFrom":subQ5}),-1.0]])]});}
            var Q38;
            {var subQ2=sQuery(id+"F4.wireOp",EDGE,"E62.top");Q38=makeQuery(id+"F4.imprint","IMPRINT",FACE,{"disambiguationData":[TD([[makeQuery(id+"F4.imprint","IMPRINT",EDGE,{"derivedFrom":subQ2}),-1.0]])]});}
            var Q39;
            {var subQ0=sQuery(id+"F4.wireOp",EDGE,"E62.bottom");Q39=makeQuery(id+"F4.imprint","IMPRINT",FACE,{"disambiguationData":[TD([[makeQuery(id+"F4.imprint","IMPRINT",EDGE,{"derivedFrom":subQ0}),1.0]])]});}
            extrude(context, id + "F6", {"entities" : qUnion([Q0, Q1, Q2, Q3, Q4, Q5, Q6, Q7, Q8, Q9, Q10, Q11, Q12, Q13, Q14, Q15, Q16, Q17, Q18, Q19, Q20, Q21, Q22, Q23, Q24, Q25, Q26, Q27, Q28, Q29, Q30, Q31, Q32, Q33, Q34, Q35, Q36, Q37, Q38, Q39]), "depth" : 4 * mm, "offsetDistance" : 25 * mm});
        }
        {
            var Q0;
            Q0=makeQuery(id+"F0.imprint","IMPRINT",FACE,{"disambiguationData":[TD([[makeQuery(id+"F0.imprint","IMPRINT",EDGE,{"derivedFrom":sQuery(id+"F0.wireOp",EDGE,"E16")}),1.0]])]});
            var Q1;
            Q1=makeQuery(id+"F0.imprint","IMPRINT",FACE,{"disambiguationData":[TD([[makeQuery(id+"F0.imprint","IMPRINT",EDGE,{"derivedFrom":sQuery(id+"F0.wireOp",EDGE,"E15")}),1.0]])]});
            extrude(context, id + "F7", {"entities" : qUnion([Q0, Q1]), "oppositeDirection" : true, "depth" : 4 * mm});
        }
        {
            var Q0;
            Q0=makeQuery(id+"F6.opExtrude","CAP_FACE",FACE,{"disambiguationData":[OSD([sQuery(id+"F0.wireOp",EDGE,"E12"),sQuery(id+"F0.wireOp",EDGE,"E19"),sQuery(id+"F4.wireOp",EDGE,"E25.1.0"),sQuery(id+"F4.wireOp",EDGE,"E25.1.1"),sQuery(id+"F4.wireOp",EDGE,"E25.2"),sQuery(id+"F4.wireOp",EDGE,"E25.3"),sQuery(id+"F4.wireOp",EDGE,"E31"),sQuery(id+"F4.wireOp",EDGE,"E32"),sQuery(id+"F4.wireOp",EDGE,"E33"),sQuery(id+"F4.wireOp",EDGE,"E34"),sQuery(id+"F4.wireOp",EDGE,"E35"),sQuery(id+"F4.wireOp",EDGE,"E36"),sQuery(id+"F4.wireOp",EDGE,"E37"),sQuery(id+"F4.wireOp",EDGE,"E39"),sQuery(id+"F4.wireOp",EDGE,"E43"),sQuery(id+"F4.wireOp",EDGE,"E45"),sQuery(id+"F4.wireOp",EDGE,"E47"),sQuery(id+"F4.wireOp",EDGE,"E48"),sQuery(id+"F4.wireOp",EDGE,"E57")])],"isStart":false});
            var sketch = newSketch(context, id + "F8", { "sketchPlane" : qUnion([Q0])});
            skCircle(sketch, "E66", {"center": v(-70.99, 23.36) * mm, "radius": 1.35 * mm});
            skCircle(sketch, "E67", {"center": v(-12.99, 23.36) * mm, "radius": 1.35 * mm});
            skSolve(sketch);
        }
        {
            var Q0;
            Q0=makeQuery(id+"F8.imprint","IMPRINT",FACE,{"disambiguationData":[TD([[makeQuery(id+"F8.imprint","IMPRINT",EDGE,{"derivedFrom":sQuery(id+"F8.wireOp",EDGE,"E67")}),1.0]])]});
            var Q1;
            Q1=makeQuery(id+"F8.imprint","IMPRINT",FACE,{"disambiguationData":[TD([[makeQuery(id+"F8.imprint","IMPRINT",EDGE,{"derivedFrom":sQuery(id+"F8.wireOp",EDGE,"E66")}),1.0]])]});
            extrude(context, id + "F9", {"entities" : qUnion([Q0, Q1]), "operationType" : NewBodyOperationType.REMOVE, "oppositeDirection" : true, "depth" : 3 * mm});
        }
        {
            var Q0;
            Q0=makeQuery(id+"F0.imprint","IMPRINT",FACE,{"disambiguationData":[TD([[makeQuery(id+"F0.imprint","IMPRINT",EDGE,{"derivedFrom":sQuery(id+"F0.wireOp",EDGE,"E1")}),1.0]])]});
            var Q1;
            Q1=makeQuery(id+"F0.imprint","IMPRINT",FACE,{"disambiguationData":[TD([[makeQuery(id+"F0.imprint","IMPRINT",EDGE,{"derivedFrom":sQuery(id+"F0.wireOp",EDGE,"E22")}),1.0]])]});
            extrude(context, id + "F10", {"entities" : qUnion([Q0, Q1]), "operationType" : NewBodyOperationType.ADD, "oppositeDirection" : true, "depth" : 3.5 * mm});
        }
        {
            var Q0;
            Q0=makeQuery(id+"F2.imprint","IMPRINT",FACE,{"disambiguationData":[TD([[makeQuery(id+"F2.imprint","IMPRINT",EDGE,{"derivedFrom":sQuery(id+"F2.wireOp",EDGE,"E24")}),-1.0]])]});
            var sketch = newSketch(context, id + "F11", { "sketchPlane" : qUnion([Q0])});
            skCircle(sketch, "E68", {"center": v(0, 0) * mm, "radius": 1.35 * mm});
            skSolve(sketch);
        }
        {
            var Q0;
            Q0=makeQuery(id+"F2.imprint","IMPRINT",FACE,{"disambiguationData":[TD([[makeQuery(id+"F2.imprint","IMPRINT",EDGE,{"derivedFrom":sQuery(id+"F2.wireOp",EDGE,"E24")}),1.0]])]});
            var Q1;
            Q1=makeQuery(id+"F11.imprint","IMPRINT",FACE,{"disambiguationData":[TD([[makeQuery(id+"F11.imprint","IMPRINT",EDGE,{"derivedFrom":sQuery(id+"F11.wireOp",EDGE,"E68")}),1.0]])]});
            extrude(context, id + "F12", {"entities" : qUnion([Q0, Q1]), "operationType" : NewBodyOperationType.REMOVE, "oppositeDirection" : true, "depth" : 2.5 * mm});
        }
    });
